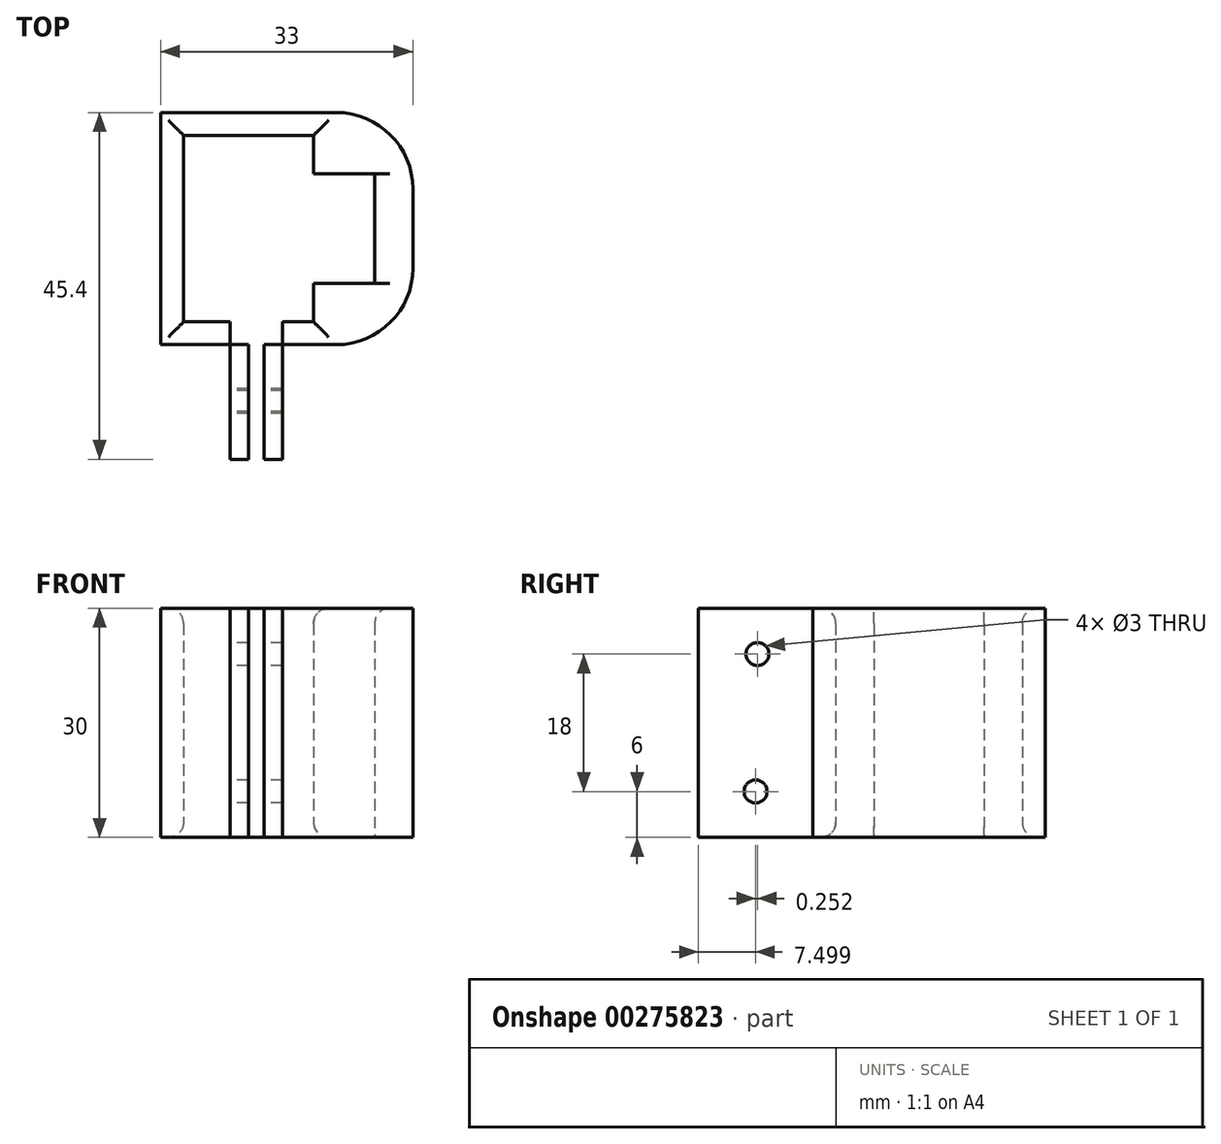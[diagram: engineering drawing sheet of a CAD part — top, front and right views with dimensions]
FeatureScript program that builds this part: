
annotation { "Feature Type Name" : "Feature", "Feature Type Description" : "" }
export const myFeature = defineFeature(function(context is Context, id is Id, definition is map)
    precondition{}
    {
        {
            var Q0;
            Q0=qCreatedBy(makeId("Top.planeOp"),FACE);
            var sketch = newSketch(context, id + "F0", { "sketchPlane" : qUnion([Q0])});
            skLineSegment(sketch, "E0.bottom", {"start": v(-12.04, 2.78) * mm, "end": v(4.96, 2.78) * mm});
            skLineSegment(sketch, "E0.top", {"start": v(-12.04, -21.62) * mm, "end": v(-3.54, -21.62) * mm});
            skLineSegment(sketch, "E0.left", {"start": v(-12.04, 2.78) * mm, "end": v(-12.04, -21.62) * mm});
            skLineSegment(sketch, "E0.right", {"start": v(4.96, 2.78) * mm, "end": v(4.96, -2.22) * mm});
            skLineSegment(sketch, "E1.bottom", {"start": v(4.96, -2.22) * mm, "end": v(12.96, -2.22) * mm});
            skLineSegment(sketch, "E1.top", {"start": v(4.96, -16.62) * mm, "end": v(12.96, -16.62) * mm});
            skLineSegment(sketch, "E1.right", {"start": v(12.96, -2.22) * mm, "end": v(12.96, -16.62) * mm});
            skLineSegment(sketch, "E2.bottom", {"start": v(-15.04, 5.78) * mm, "end": v(17.96, 5.78) * mm});
            skLineSegment(sketch, "E2.top", {"start": v(-15.04, -24.62) * mm, "end": v(-3.54, -24.62) * mm});
            skLineSegment(sketch, "E2.left", {"start": v(-15.04, 5.78) * mm, "end": v(-15.04, -24.62) * mm});
            skLineSegment(sketch, "E2.right", {"start": v(17.96, 5.78) * mm, "end": v(17.96, -24.62) * mm});
            skLineSegment(sketch, "E3.left", {"start": v(-3.54, -21.62) * mm, "end": v(-3.54, -24.62) * mm});
            skLineSegment(sketch, "E3.right", {"start": v(-1.5, -21.62) * mm, "end": v(-1.5, -24.62) * mm});
            skLineSegment(sketch, "E4.trimOffspring", {"start": v(-1.5, -21.62) * mm, "end": v(4.96, -21.62) * mm});
            skLineSegment(sketch, "E5.trimOffspring", {"start": v(-1.5, -24.62) * mm, "end": v(17.96, -24.62) * mm});
            skLineSegment(sketch, "E6.trimOffspring", {"start": v(4.96, -16.62) * mm, "end": v(4.96, -21.62) * mm});
            skLineSegment(sketch, "E7.bottom", {"start": v(-3.54, -21.62) * mm, "end": v(-5.94, -21.62) * mm});
            skLineSegment(sketch, "E7.top", {"start": v(-3.54, -39.62) * mm, "end": v(-5.94, -39.62) * mm});
            skLineSegment(sketch, "E7.left", {"start": v(-3.54, -21.62) * mm, "end": v(-3.54, -39.62) * mm});
            skLineSegment(sketch, "E7.right", {"start": v(-5.94, -21.62) * mm, "end": v(-5.94, -39.62) * mm});
            skLineSegment(sketch, "E8.bottom", {"start": v(-1.5, -21.62) * mm, "end": v(0.9, -21.62) * mm});
            skLineSegment(sketch, "E8.top", {"start": v(-1.5, -39.62) * mm, "end": v(0.9, -39.62) * mm});
            skLineSegment(sketch, "E8.left", {"start": v(-1.5, -21.62) * mm, "end": v(-1.5, -39.62) * mm});
            skLineSegment(sketch, "E8.right", {"start": v(0.9, -21.62) * mm, "end": v(0.9, -39.62) * mm});
            skSolve(sketch);
        }
        {
            var Q0;
            Q0=makeQuery(id+"F0.imprint","IMPRINT",FACE,{"disambiguationData":[TD([[makeQuery(id+"F0.imprint","IMPRINT",EDGE,{"derivedFrom":sQuery(id+"F0.wireOp",EDGE,"E0.bottom")}),1.0]])]});
            var Q1;
            {var subQ5=sQuery(id+"F0.wireOp",EDGE,"E8.bottom");Q1=makeQuery(id+"F0.imprint","IMPRINT",FACE,{"disambiguationData":[TD([[makeQuery(id+"F0.imprint","IMPRINT",EDGE,{"derivedFrom":subQ5}),-1.0]])]});}
            var Q2;
            {var subQ5=sQuery(id+"F0.wireOp",EDGE,"E8.top");Q2=makeQuery(id+"F0.imprint","IMPRINT",FACE,{"disambiguationData":[TD([[makeQuery(id+"F0.imprint","IMPRINT",EDGE,{"derivedFrom":subQ5}),1.0]])]});}
            var Q3;
            {var subQ5=sQuery(id+"F0.wireOp",EDGE,"E7.bottom");Q3=makeQuery(id+"F0.imprint","IMPRINT",FACE,{"disambiguationData":[TD([[makeQuery(id+"F0.imprint","IMPRINT",EDGE,{"derivedFrom":subQ5}),1.0]])]});}
            var Q4;
            {var subQ5=sQuery(id+"F0.wireOp",EDGE,"E7.top");Q4=makeQuery(id+"F0.imprint","IMPRINT",FACE,{"disambiguationData":[TD([[makeQuery(id+"F0.imprint","IMPRINT",EDGE,{"derivedFrom":subQ5}),-1.0]])]});}
            extrude(context, id + "F1", {"entities" : qUnion([Q0, Q1, Q2, Q3, Q4]), "depth" : 30 * mm});
        }
        {
            var Q0;
            Q0=makeQuery(id+"F1.opExtrude","SWEPT_FACE",FACE,{"disambiguationData":[OSD([sQuery(id+"F0.wireOp",EDGE,"E7.right")])]});
            var sketch = newSketch(context, id + "F2", { "sketchPlane" : qUnion([Q0])});
            skCircle(sketch, "E9", {"center": v(31.87, 24) * mm, "radius": 1.5 * mm});
            skCircle(sketch, "E10", {"center": v(32.12, 6) * mm, "radius": 1.5 * mm});
            skPoint(sketch, "E10.centerSnap0", {"position": v(32.12, 30) * mm});
            skSolve(sketch);
        }
        {
            var Q0;
            Q0=makeQuery(id+"F2.imprint","IMPRINT",FACE,{"disambiguationData":[TD([[makeQuery(id+"F2.imprint","IMPRINT",EDGE,{"derivedFrom":sQuery(id+"F2.wireOp",EDGE,"E10")}),1.0]])]});
            var Q1;
            Q1=makeQuery(id+"F2.imprint","IMPRINT",FACE,{"disambiguationData":[TD([[makeQuery(id+"F2.imprint","IMPRINT",EDGE,{"derivedFrom":sQuery(id+"F2.wireOp",EDGE,"E9")}),1.0]])]});
            extrude(context, id + "F3", {"entities" : qUnion([Q0, Q1]), "operationType" : NewBodyOperationType.REMOVE, "oppositeDirection" : true, "depth" : 25 * mm});
        }
        {
            var Q0;
            Q0=makeQuery(id+"F1.opExtrude","CAP_EDGE",EDGE,{"disambiguationData":[OSD([sQuery(id+"F0.wireOp",EDGE,"E0.left")])],"isStart":false});
            var Q1;
            Q1=makeQuery(id+"F1.opExtrude","CAP_EDGE",EDGE,{"disambiguationData":[OSD([sQuery(id+"F0.wireOp",EDGE,"E0.bottom")])],"isStart":false});
            var Q2;
            Q2=makeQuery(id+"F1.opExtrude","CAP_EDGE",EDGE,{"disambiguationData":[OSD([sQuery(id+"F0.wireOp",EDGE,"E0.right")])],"isStart":false});
            var Q3;
            Q3=makeQuery(id+"F1.opExtrude","CAP_EDGE",EDGE,{"disambiguationData":[OSD([sQuery(id+"F0.wireOp",EDGE,"E6.trimOffspring")])],"isStart":false});
            var Q4;
            Q4=makeQuery(id+"F1.opExtrude","CAP_EDGE",EDGE,{"disambiguationData":[OSD([sQuery(id+"F0.wireOp",EDGE,"E4.trimOffspring"),sQuery(id+"F0.wireOp",EDGE,"E8.bottom")])],"isStart":false});
            var Q5;
            Q5=makeQuery(id+"F1.opExtrude","CAP_EDGE",EDGE,{"disambiguationData":[OSD([sQuery(id+"F0.wireOp",EDGE,"E0.top"),sQuery(id+"F0.wireOp",EDGE,"E7.bottom")])],"isStart":false});
            var Q6;
            Q6=makeQuery(id+"F1.opExtrude","CAP_EDGE",EDGE,{"disambiguationData":[OSD([sQuery(id+"F0.wireOp",EDGE,"E1.right")])],"isStart":false});
            var Q7;
            Q7=makeQuery(id+"F1.opExtrude","CAP_EDGE",EDGE,{"disambiguationData":[OSD([sQuery(id+"F0.wireOp",EDGE,"E0.bottom")])],"isStart":true});
            var Q8;
            Q8=makeQuery(id+"F1.opExtrude","CAP_EDGE",EDGE,{"disambiguationData":[OSD([sQuery(id+"F0.wireOp",EDGE,"E0.left")])],"isStart":true});
            var Q9;
            Q9=makeQuery(id+"F1.opExtrude","CAP_EDGE",EDGE,{"disambiguationData":[OSD([sQuery(id+"F0.wireOp",EDGE,"E0.top"),sQuery(id+"F0.wireOp",EDGE,"E7.bottom")])],"isStart":true});
            var Q10;
            Q10=makeQuery(id+"F1.opExtrude","CAP_EDGE",EDGE,{"disambiguationData":[OSD([sQuery(id+"F0.wireOp",EDGE,"E4.trimOffspring"),sQuery(id+"F0.wireOp",EDGE,"E8.bottom")])],"isStart":true});
            var Q11;
            Q11=makeQuery(id+"F1.opExtrude","CAP_EDGE",EDGE,{"disambiguationData":[OSD([sQuery(id+"F0.wireOp",EDGE,"E6.trimOffspring")])],"isStart":true});
            var Q12;
            Q12=makeQuery(id+"F1.opExtrude","CAP_EDGE",EDGE,{"disambiguationData":[OSD([sQuery(id+"F0.wireOp",EDGE,"E0.right")])],"isStart":true});
            fillet(context, id + "F4", {"entities" : qUnion([Q0, Q1, Q2, Q3, Q4, Q5, Q6, Q7, Q8, Q9, Q10, Q11, Q12]), "radius" : 2 * mm, "tangentPropagation" : true, "allowEdgeOverflow" : false});
        }
        {
            var Q0;
            Q0=makeQuery(id+"F1.opExtrude","SWEPT_EDGE",EDGE,{"disambiguationData":[OSD([sQuery(id+"F0.wireOp",EDGE,"E2.bottom"),sQuery(id+"F0.wireOp",EDGE,"E2.right")])]});
            var Q1;
            Q1=makeQuery(id+"F1.opExtrude","SWEPT_EDGE",EDGE,{"disambiguationData":[OSD([sQuery(id+"F0.wireOp",EDGE,"E2.right"),sQuery(id+"F0.wireOp",EDGE,"E5.trimOffspring")])]});
            fillet(context, id + "F5", {"entities" : qUnion([Q0, Q1]), "radius" : 10 * mm, "tangentPropagation" : true, "allowEdgeOverflow" : false});
        }
    });
